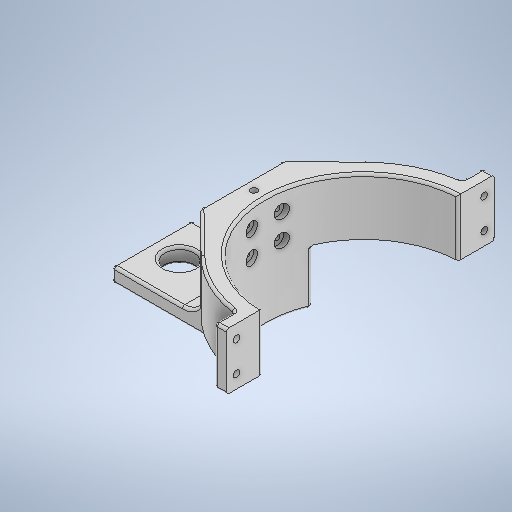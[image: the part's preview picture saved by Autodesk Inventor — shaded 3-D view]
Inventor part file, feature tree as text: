
AUTODESK INVENTOR PART (.ipt)
format: ipt  version: 2025.1 (Build 291241000, 241)  size: 566,784 bytes
history: native  units: mm
features: extrude x8, sketch x8, fillet x4, other x2
ambient origin geometry x8: Origin, YZ Plane, XZ Plane, XY Plane, X Axis, Y Axis, Z Axis, Center Point
bodies: Solide1 (feature_tree)
feature tree (22):
  extrude  "Extrusion1"  Depth=137.383mm
  fillet  "Congé2"  Radius=117.383mm
  fillet  "Congé3"  Radius=2.0mm
  extrude  "Extrusion2"  Depth=7.0mm
  extrude  "Extrusion3"  Depth=160.0mm
  extrude  "Extrusion4"  Depth=25.887mm
  other  "Plan de construction1"
  extrude  "Extrusion5"  Depth=14.0mm
  extrude  "Extrusion11"  Depth=1.0mm
  extrude  "Extrusion12"  Depth=34.0mm TaperAngle=0.0deg
  fillet  "Congé6"  Radius=2.0mm
  fillet  "Congé5"  Radius=3.0mm
  extrude  "Extrusion13"  Depth=6.0mm
  sketch  "Esquisse1"
  sketch  "Esquisse2"
  sketch  "Esquisse3"
  other  "Réseau d'esquisse circulaire1"
  sketch  "Esquisse4"
  sketch  "Esquisse5"
  sketch  "Esquisse13"
  sketch  "Esquisse14"
  sketch  "Esquisse15"
